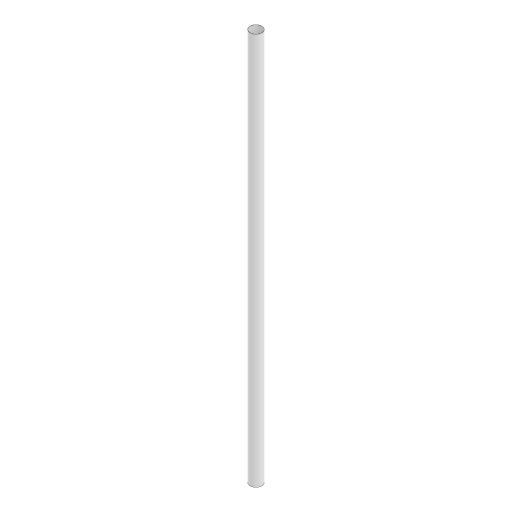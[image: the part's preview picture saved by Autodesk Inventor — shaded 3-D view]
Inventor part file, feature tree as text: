
AUTODESK INVENTOR PART (.ipt)
format: ipt  version: 2024.3 (Build 283343000, 343)  size: 82,944 bytes
history: native  units: mm
features: extrude x1, sketch x1
ambient origin geometry x8: Origin, YZ Plane, XZ Plane, XY Plane, X Axis, Y Axis, Z Axis, Center Point
bodies: Solid1 (feature_tree)
feature tree (2):
  extrude  "Extrusion1"  Depth=140.0mm
  sketch  "Sketch1"  dims[d0=4.1mm d1=4.2mm d2=140.0mm d3=0.0mm]
